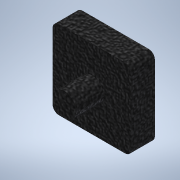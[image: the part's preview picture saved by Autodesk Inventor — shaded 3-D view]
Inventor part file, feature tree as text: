
AUTODESK INVENTOR PART (.ipt)
format: ipt  version: 2021.3 (Build 253353000, 353)  size: 105,984 bytes
history: native  units: mm
features: sketch x1, imported_body x1
ambient origin geometry x8: Origin, YZ Plane, XZ Plane, XY Plane, X Axis, Y Axis, Z Axis, Center Point
bodies: Volumenkörper1 (feature_tree)
feature tree (2):
  sketch  "Skizze1"
  imported_body  "Basis1"
